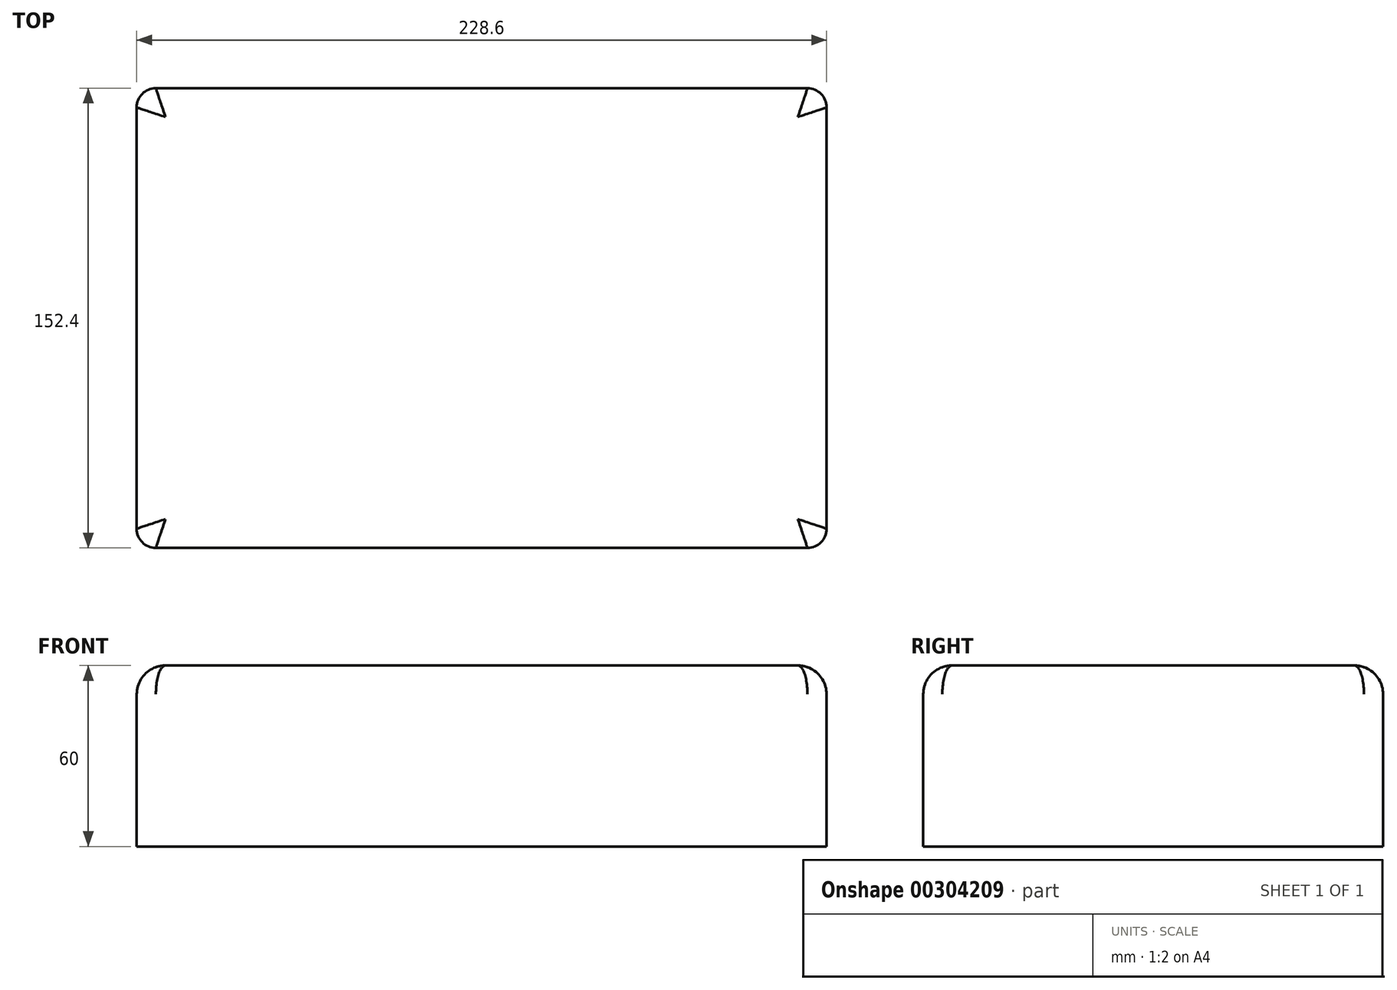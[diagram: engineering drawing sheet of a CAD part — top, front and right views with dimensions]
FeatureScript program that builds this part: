
annotation { "Feature Type Name" : "Feature", "Feature Type Description" : "" }
export const myFeature = defineFeature(function(context is Context, id is Id, definition is map)
    precondition{}
    {
        {
            var Q0;
            Q0=qCreatedBy(makeId("Top.planeOp"),FACE);
            var sketch = newSketch(context, id + "F0", { "sketchPlane" : qUnion([Q0])});
            skLineSegment(sketch, "E0.bottom", {"start": v(6.35, 0) * mm, "end": v(222.25, 0) * mm});
            skLineSegment(sketch, "E0.top", {"start": v(6.35, 152.4) * mm, "end": v(222.25, 152.4) * mm});
            skLineSegment(sketch, "E0.left", {"start": v(0, 6.35) * mm, "end": v(0, 146.05) * mm});
            skLineSegment(sketch, "E0.right", {"start": v(228.6, 6.35) * mm, "end": v(228.6, 146.05) * mm});
            skPoint(sketch, "E1.visualSharp", {"position": v(0, 152.4) * mm});
            skArc(sketch, "E1.filletArc", {"start": v(6.35, 152.4) * mm, "mid": v(1.86, 150.54) * mm, "end": v(0, 146.05) * mm});
            skPoint(sketch, "E2.visualSharp", {"position": v(228.6, 152.4) * mm});
            skArc(sketch, "E2.filletArc", {"start": v(228.6, 146.05) * mm, "mid": v(226.74, 150.54) * mm, "end": v(222.25, 152.4) * mm});
            skPoint(sketch, "E3.visualSharp", {"position": v(228.6, 0) * mm});
            skArc(sketch, "E3.filletArc", {"start": v(222.25, 0) * mm, "mid": v(226.74, 1.86) * mm, "end": v(228.6, 6.35) * mm});
            skPoint(sketch, "E4.visualSharp", {"position": v(0, 0) * mm});
            skArc(sketch, "E4.filletArc", {"start": v(0, 6.35) * mm, "mid": v(1.86, 1.86) * mm, "end": v(6.35, 0) * mm});
            skSolve(sketch);
        }
        {
            var Q0;
            Q0=makeQuery(id+"F0.imprint","IMPRINT",FACE,{"disambiguationData":[TD([[makeQuery(id+"F0.imprint","IMPRINT",EDGE,{"derivedFrom":sQuery(id+"F0.wireOp",EDGE,"E0.bottom")}),1.0]])]});
            extrude(context, id + "F1", {"entities" : qUnion([Q0]), "depth" : 60 * mm});
        }
        {
            var Q0;
            Q0=makeQuery(id+"F1.opExtrude","CAP_EDGE",EDGE,{"disambiguationData":[OSD([sQuery(id+"F0.wireOp",EDGE,"E0.bottom")])],"isStart":false});
            fillet(context, id + "F2", {"entities" : qUnion([Q0]), "radius" : 9.52 * mm, "tangentPropagation" : true, "allowEdgeOverflow" : false});
        }
    });
